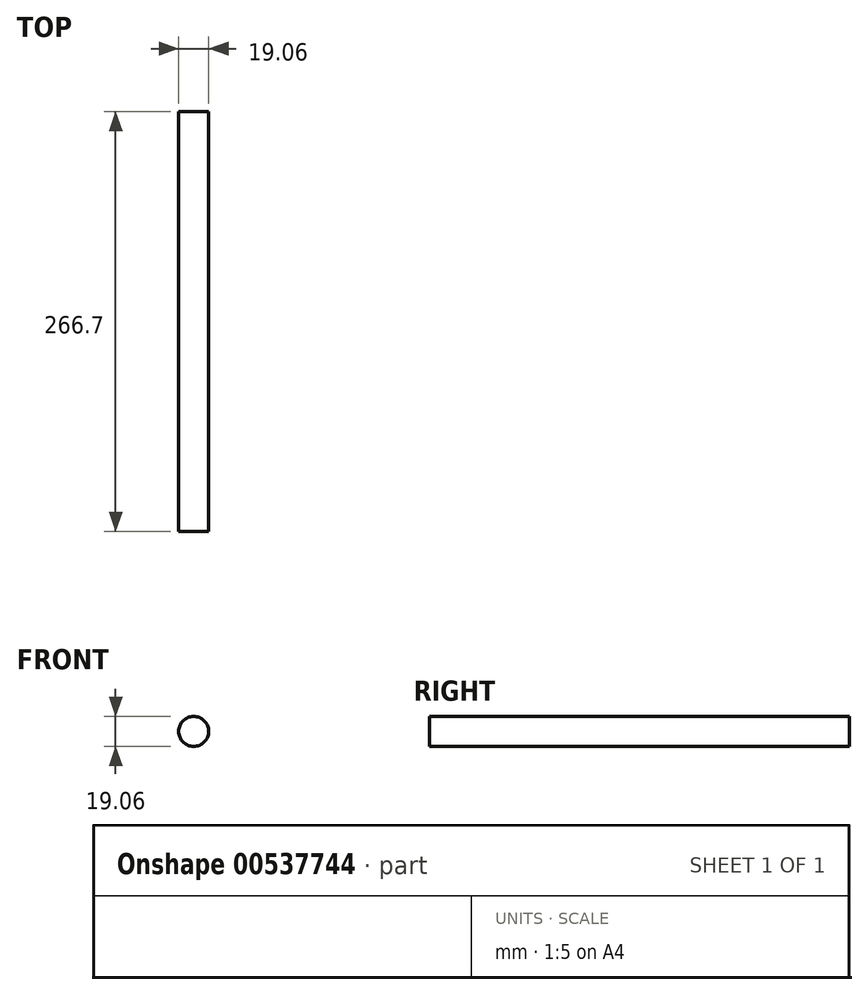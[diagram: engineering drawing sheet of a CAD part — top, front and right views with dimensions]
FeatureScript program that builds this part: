
annotation { "Feature Type Name" : "Feature", "Feature Type Description" : "" }
export const myFeature = defineFeature(function(context is Context, id is Id, definition is map)
    precondition{}
    {
        {
            var Q0;
            Q0=qCreatedBy(makeId("Front.planeOp"),FACE);
            var sketch = newSketch(context, id + "F0", { "sketchPlane" : qUnion([Q0])});
            skCircle(sketch, "E0", {"center": v(0, 0) * mm, "radius": 9.53 * mm});
            skSolve(sketch);
        }
        {
            var Q0;
            Q0=makeQuery(id+"F0.imprint","IMPRINT",FACE,{"disambiguationData":[TD([[makeQuery(id+"F0.imprint","IMPRINT",EDGE,{"derivedFrom":sQuery(id+"F0.wireOp",EDGE,"E0")}),1.0]])]});
            extrude(context, id + "F1", {"entities" : qUnion([Q0]), "depth" : 266.7 * mm, "offsetDistance" : 25.4 * mm});
        }
        {
            var Q0;
            Q0=qCreatedBy(makeId("Front.planeOp"),FACE);
            var sketch = newSketch(context, id + "F2", { "sketchPlane" : qUnion([Q0])});
            skCircle(sketch, "E1", {"center": v(0, 0) * mm, "radius": 8.26 * mm});
            skSolve(sketch);
        }
        {
            var Q0;
            Q0=sQuery(id+"F2.wireOp",EDGE,"E1");
            extrude(context, id + "F3", {"bodyType" : ToolBodyType.SURFACE, "surfaceEntities" : qUnion([Q0]), "depth" : 266.7 * mm, "offsetDistance" : 25.4 * mm});
        }
    });
